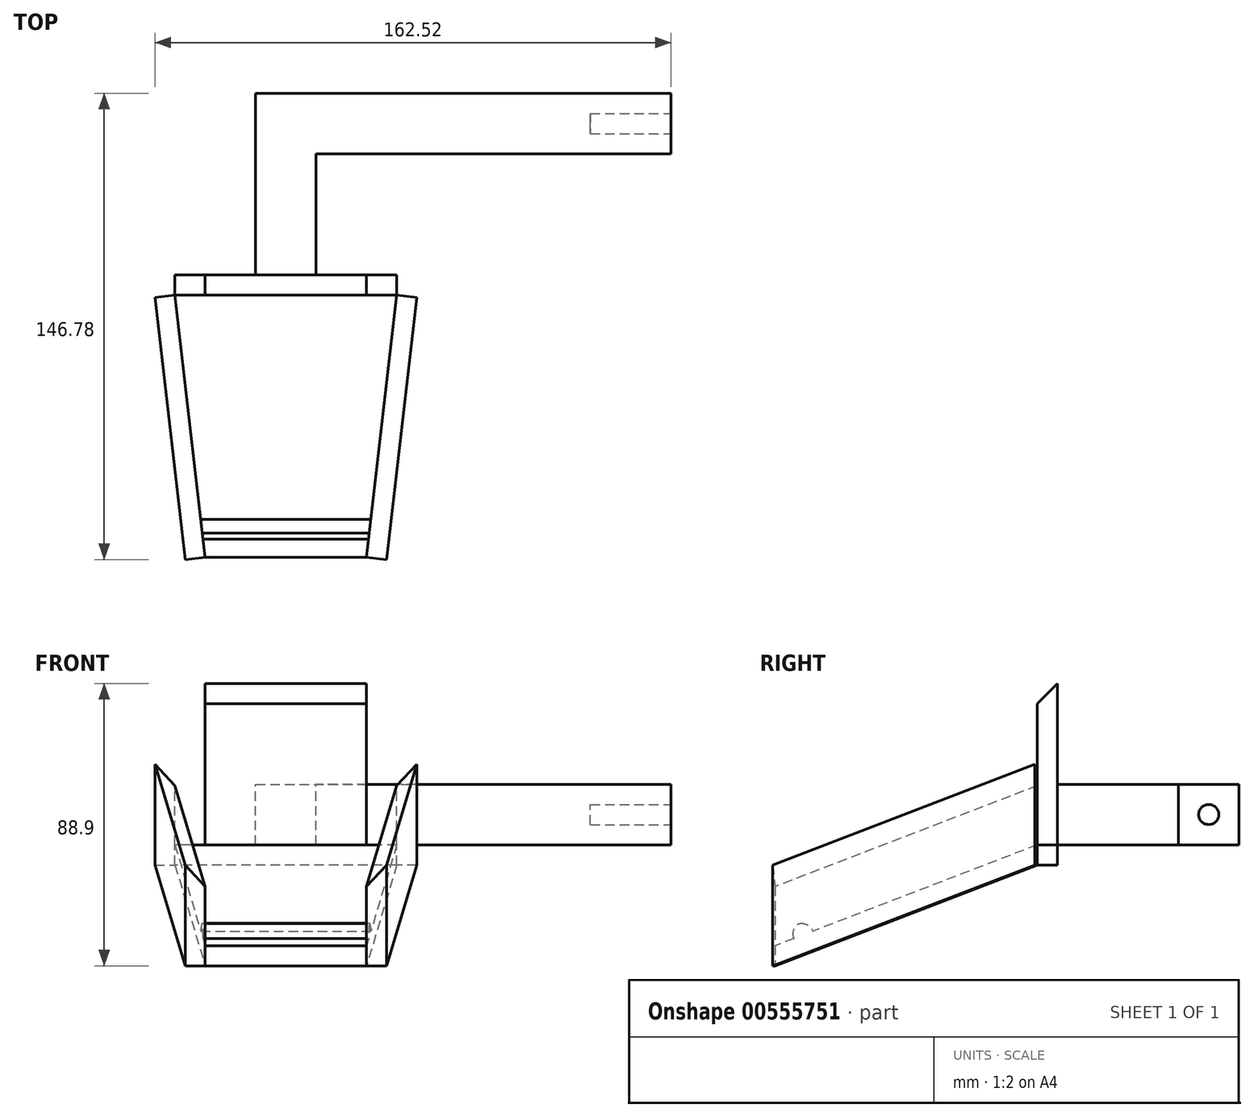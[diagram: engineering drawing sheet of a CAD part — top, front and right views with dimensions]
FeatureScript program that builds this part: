
annotation { "Feature Type Name" : "Feature", "Feature Type Description" : "" }
export const myFeature = defineFeature(function(context is Context, id is Id, definition is map)
    precondition{}
    {
        {
            var Q0;
            Q0=qCreatedBy(makeId("Front.planeOp"),FACE);
            var sketch = newSketch(context, id + "F0", { "sketchPlane" : qUnion([Q0])});
            skLineSegment(sketch, "E0.bottom", {"start": v(0, 0) * mm, "end": v(-69.85, 0) * mm});
            skLineSegment(sketch, "E0.top", {"start": v(0, 6.35) * mm, "end": v(-69.85, 6.35) * mm});
            skLineSegment(sketch, "E0.left", {"start": v(0, 0) * mm, "end": v(0, 6.35) * mm});
            skLineSegment(sketch, "E0.right", {"start": v(-69.85, 0) * mm, "end": v(-69.85, 6.35) * mm});
            skSolve(sketch);
        }
        {
            var Q0;
            Q0=makeQuery(id+"F0.imprint","IMPRINT",FACE,{"disambiguationData":[TD([[makeQuery(id+"F0.imprint","IMPRINT",EDGE,{"derivedFrom":sQuery(id+"F0.wireOp",EDGE,"E0.bottom")}),-1.0]])]});
            cPlane(context, id + "F1", {"entities" : qUnion([Q0]), "cplaneType" : CPlaneType.OFFSET, "offset" : 82.55 * mm, "width" : 152.4 * mm, "height" : 152.4 * mm});
        }
        {
            var Q0;
            Q0=qCreatedBy(id+"F1.planeOp",FACE);
            var sketch = newSketch(context, id + "F2", { "sketchPlane" : qUnion([Q0])});
            skLineSegment(sketch, "E1.bottom", {"start": v(-60.33, -25.4) * mm, "end": v(-9.52, -25.4) * mm});
            skLineSegment(sketch, "E1.top", {"start": v(-60.33, -31.75) * mm, "end": v(-9.52, -31.75) * mm});
            skLineSegment(sketch, "E1.left", {"start": v(-60.33, -25.4) * mm, "end": v(-60.33, -31.75) * mm});
            skLineSegment(sketch, "E1.right", {"start": v(-9.53, -25.4) * mm, "end": v(-9.52, -31.75) * mm});
            skSolve(sketch);
        }
        {
            var Q0;
            Q0=makeQuery(id+"F0.imprint","IMPRINT",FACE,{"disambiguationData":[TD([[makeQuery(id+"F0.imprint","IMPRINT",EDGE,{"derivedFrom":sQuery(id+"F0.wireOp",EDGE,"E0.bottom")}),-1.0]])]});
            var Q1;
            Q1=makeQuery(id+"F2.imprint","IMPRINT",FACE,{"disambiguationData":[TD([[makeQuery(id+"F2.imprint","IMPRINT",EDGE,{"derivedFrom":sQuery(id+"F2.wireOp",EDGE,"E1.bottom")}),-1.0]])]});
            loft(context, id + "F3", {"sheetProfilesArray" : [{ "sheetProfileEntities" : qUnion([Q0]) }, { "sheetProfileEntities" : qUnion([Q1]) }]});
        }
        {
            var Q0;
            Q0=makeQuery(id+"F3.opLoft","SWEPT_FACE",FACE,{"disambiguationData":[OSD([sQuery(id+"F0.wireOp",EDGE,"E0.bottom"),sQuery(id+"F0.wireOp",EDGE,"E0.top"),sQuery(id+"F0.wireOp",EDGE,"E0.right"),sQuery(id+"F2.wireOp",EDGE,"E1.bottom"),sQuery(id+"F2.wireOp",EDGE,"E1.top"),sQuery(id+"F2.wireOp",EDGE,"E1.left")])]});
            var sketch = newSketch(context, id + "F4", { "sketchPlane" : qUnion([Q0])});
            skLineSegment(sketch, "E2", {"start": v(-8, 6.35) * mm, "end": v(-8, 31.75) * mm});
            skLineSegment(sketch, "E3", {"start": v(75.1, -25.4) * mm, "end": v(75.1, 0) * mm});
            skLineSegment(sketch, "E4", {"start": v(75.1, 0) * mm, "end": v(-8, 31.75) * mm});
            skLineSegment(sketch, "E5", {"start": v(-8, 0) * mm, "end": v(-8, 6.35) * mm});
            skLineSegment(sketch, "E6", {"start": v(-8, 0) * mm, "end": v(75.1, -31.75) * mm});
            skLineSegment(sketch, "E7", {"start": v(75.1, -31.75) * mm, "end": v(75.1, -25.4) * mm});
            skSolve(sketch);
        }
        {
            var Q0;
            Q0=makeQuery(id+"F4.imprint","IMPRINT",FACE,{"disambiguationData":[TD([[makeQuery(id+"F4.imprint","IMPRINT",EDGE,{"derivedFrom":sQuery(id+"F4.wireOp",EDGE,"E5")}),1.0]])]});
            var Q1;
            Q1=makeQuery(id+"F4.imprint","IMPRINT",FACE,{"disambiguationData":[TD([[makeQuery(id+"F4.imprint","IMPRINT",EDGE,{"derivedFrom":sQuery(id+"F4.wireOp",EDGE,"E2")}),-1.0]])]});
            extrude(context, id + "F5", {"entities" : qUnion([Q0, Q1]), "operationType" : NewBodyOperationType.ADD, "depth" : 6.35 * mm, "offsetDistance" : 25.4 * mm});
        }
        {
            var Q0;
            Q0=makeQuery(id+"F3.opLoft","SWEPT_FACE",FACE,{"disambiguationData":[OSD([sQuery(id+"F0.wireOp",EDGE,"E0.bottom"),sQuery(id+"F0.wireOp",EDGE,"E0.top"),sQuery(id+"F0.wireOp",EDGE,"E0.left"),sQuery(id+"F2.wireOp",EDGE,"E1.bottom"),sQuery(id+"F2.wireOp",EDGE,"E1.top"),sQuery(id+"F2.wireOp",EDGE,"E1.right")])]});
            var sketch = newSketch(context, id + "F6", { "sketchPlane" : qUnion([Q0])});
            skLineSegment(sketch, "E8", {"start": v(-83.1, -31.75) * mm, "end": v(0, 0) * mm});
            skLineSegment(sketch, "E9", {"start": v(0, 0) * mm, "end": v(0, 31.75) * mm});
            skLineSegment(sketch, "E10", {"start": v(0, 31.75) * mm, "end": v(-83.1, 0) * mm});
            skLineSegment(sketch, "E11", {"start": v(-83.1, 0) * mm, "end": v(-83.1, -31.75) * mm});
            skSolve(sketch);
        }
        {
            var Q0;
            {var subQ2=sQuery(id+"F6.wireOp",EDGE,"E10");Q0=makeQuery(id+"F6.imprint","IMPRINT",FACE,{"disambiguationData":[TD([[makeQuery(id+"F6.imprint","IMPRINT",EDGE,{"derivedFrom":subQ2}),1.0]])]});}
            var Q1;
            {var subQ0=sQuery(id+"F6.wireOp",EDGE,"E8");Q1=makeQuery(id+"F6.imprint","IMPRINT",FACE,{"disambiguationData":[TD([[makeQuery(id+"F6.imprint","IMPRINT",EDGE,{"derivedFrom":subQ0}),-1.0]])]});}
            extrude(context, id + "F7", {"entities" : qUnion([Q0, Q1]), "operationType" : NewBodyOperationType.ADD, "depth" : 6.35 * mm, "offsetDistance" : 25.4 * mm});
        }
        {
            var Q0;
            Q0=makeQuery(id+"F3.opLoft","SWEPT_FACE",FACE,{"disambiguationData":[OSD([sQuery(id+"F0.wireOp",EDGE,"E0.top"),sQuery(id+"F0.wireOp",EDGE,"E0.left"),sQuery(id+"F0.wireOp",EDGE,"E0.right"),sQuery(id+"F2.wireOp",EDGE,"E1.bottom"),sQuery(id+"F2.wireOp",EDGE,"E1.left"),sQuery(id+"F2.wireOp",EDGE,"E1.right")])]});
            var sketch = newSketch(context, id + "F8", { "sketchPlane" : qUnion([Q0])});
            skLineSegment(sketch, "E12", {"start": v(-60.33, -86.17) * mm, "end": v(-61.7, -73.47) * mm});
            skLineSegment(sketch, "E13", {"start": v(-61.7, -73.47) * mm, "end": v(-8.16, -73.47) * mm});
            skLineSegment(sketch, "E14", {"start": v(-8.16, -73.47) * mm, "end": v(-9.53, -86.17) * mm});
            skLineSegment(sketch, "E15", {"start": v(-61, -79.82) * mm, "end": v(-8.84, -79.82) * mm});
            skSolve(sketch);
        }
        {
            var Q0;
            {var subQ0=sQuery(id+"F8.wireOp",EDGE,"E13");Q0=makeQuery(id+"F8.imprint","IMPRINT",FACE,{"disambiguationData":[TD([[makeQuery(id+"F8.imprint","IMPRINT",EDGE,{"derivedFrom":subQ0}),-1.0]])]});}
            extrude(context, id + "F9", {"entities" : qUnion([Q0]), "operationType" : NewBodyOperationType.ADD, "depth" : 3.84 * mm, "offsetDistance" : 25.4 * mm});
        }
        {
            var Q0;
            Q0=makeQuery(id+"F9.opExtrude","CAP_EDGE",EDGE,{"disambiguationData":[OSD([sQuery(id+"F8.wireOp",EDGE,"E15")])],"isStart":false});
            var Q1;
            Q1=makeQuery(id+"F9.opExtrude","CAP_EDGE",EDGE,{"disambiguationData":[OSD([sQuery(id+"F8.wireOp",EDGE,"E13")])],"isStart":false});
            fillet(context, id + "F10", {"entities" : qUnion([Q0, Q1]), "radius" : 3.8 * mm, "tangentPropagation" : true, "allowEdgeOverflow" : false});
        }
        {
            var Q0;
            Q0=makeQuery(id+"F3.opLoft","CAP_FACE",FACE,{"disambiguationData":[OSD([makeQuery(id+"F0.imprint","IMPRINT",FACE,{"disambiguationData":[TD([[makeQuery(id+"F0.imprint","IMPRINT",EDGE,{"derivedFrom":sQuery(id+"F0.wireOp",EDGE,"E0.bottom")}),-1.0]])]})])],"isStart":true});
            var sketch = newSketch(context, id + "F11", { "sketchPlane" : qUnion([Q0])});
            skLineSegment(sketch, "E16.bottom", {"start": v(0, 0) * mm, "end": v(76.2, 0) * mm});
            skLineSegment(sketch, "E16.top", {"start": v(0, 44.45) * mm, "end": v(76.2, 44.45) * mm});
            skLineSegment(sketch, "E16.left", {"start": v(0, 0) * mm, "end": v(0, 44.45) * mm});
            skLineSegment(sketch, "E16.right", {"start": v(76.2, 0) * mm, "end": v(76.2, 44.45) * mm});
            skSolve(sketch);
        }
        {
            var Q0;
            {var subQ0=sQuery(id+"F11.wireOp",EDGE,"E16.bottom");Q0=makeQuery(id+"F11.imprint","IMPRINT",FACE,{"disambiguationData":[TD([[makeQuery(id+"F11.imprint","IMPRINT",EDGE,{"derivedFrom":subQ0}),-1.0]])]});}
            extrude(context, id + "F12", {"entities" : qUnion([Q0]), "operationType" : NewBodyOperationType.ADD, "depth" : 6.35 * mm, "offsetDistance" : 25.4 * mm});
        }
        {
            var Q0;
            Q0=makeQuery(id+"F12.opExtrude","SWEPT_FACE",FACE,{"disambiguationData":[OSD([sQuery(id+"F0.wireOp",EDGE,"E0.top"),sQuery(id+"F0.wireOp",EDGE,"E0.left"),sQuery(id+"F0.wireOp",EDGE,"E0.right")])]});
            var sketch = newSketch(context, id + "F13", { "sketchPlane" : qUnion([Q0])});
            skLineSegment(sketch, "E17.bottom", {"start": v(-9.52, 0) * mm, "end": v(-60.33, 0) * mm});
            skLineSegment(sketch, "E17.top", {"start": v(-9.53, 6.35) * mm, "end": v(-60.33, 6.35) * mm});
            skLineSegment(sketch, "E17.left", {"start": v(-60.33, 6.35) * mm, "end": v(-60.33, 0) * mm});
            skLineSegment(sketch, "E17.right", {"start": v(-9.53, 6.35) * mm, "end": v(-9.52, 0) * mm});
            skSolve(sketch);
        }
        {
            var Q0;
            Q0=makeQuery(id+"F13.imprint","IMPRINT",FACE,{"disambiguationData":[TD([[makeQuery(id+"F13.imprint","IMPRINT",EDGE,{"derivedFrom":sQuery(id+"F13.wireOp",EDGE,"E17.bottom")}),-1.0]])]});
            extrude(context, id + "F14", {"entities" : qUnion([Q0]), "operationType" : NewBodyOperationType.ADD, "depth" : 50.8 * mm, "offsetDistance" : 25.4 * mm});
        }
        {
            var Q0;
            Q0=makeQuery(id+"F14.opExtrude","CAP_EDGE",EDGE,{"disambiguationData":[OSD([sQuery(id+"F13.wireOp",EDGE,"E17.bottom")])],"isStart":false});
            chamfer(context, id + "F15", {"entities" : qUnion([Q0]), "width" : 6.35 * mm, "tangentPropagation" : true});
        }
        {
            var Q0;
            Q0=makeQuery(id+"F14.boolean.opBoolean","MERGE",FACE,{"derivedFrom":[makeQuery(id+"F12.opExtrude","CAP_FACE",FACE,{"disambiguationData":[OSD([sQuery(id+"F0.wireOp",EDGE,"E0.top"),sQuery(id+"F0.wireOp",EDGE,"E0.left"),sQuery(id+"F0.wireOp",EDGE,"E0.right"),sQuery(id+"F11.wireOp",EDGE,"E16.bottom"),sQuery(id+"F11.wireOp",EDGE,"E16.left"),sQuery(id+"F11.wireOp",EDGE,"E16.right")])],"isStart":false}),makeQuery(id+"F14.opExtrude","SWEPT_FACE",FACE,{"disambiguationData":[OSD([sQuery(id+"F13.wireOp",EDGE,"E17.top")])]})]});
            var sketch = newSketch(context, id + "F16", { "sketchPlane" : qUnion([Q0])});
            skLineSegment(sketch, "E18.bottom", {"start": v(44.45, 6.35) * mm, "end": v(25.4, 6.35) * mm});
            skLineSegment(sketch, "E18.top", {"start": v(44.45, 25.4) * mm, "end": v(25.4, 25.4) * mm});
            skLineSegment(sketch, "E18.left", {"start": v(44.45, 6.35) * mm, "end": v(44.45, 25.4) * mm});
            skLineSegment(sketch, "E18.right", {"start": v(25.4, 6.35) * mm, "end": v(25.4, 25.4) * mm});
            skPoint(sketch, "E18.middle", {"position": v(34.92, 15.88) * mm});
            skSolve(sketch);
        }
        {
            var Q0;
            Q0=makeQuery(id+"F16.imprint","IMPRINT",FACE,{"disambiguationData":[TD([[makeQuery(id+"F16.imprint","IMPRINT",EDGE,{"derivedFrom":sQuery(id+"F16.wireOp",EDGE,"E18.bottom")}),-1.0]])]});
            extrude(context, id + "F17", {"entities" : qUnion([Q0]), "operationType" : NewBodyOperationType.ADD, "depth" : 57.15 * mm, "offsetDistance" : 25.4 * mm});
        }
        {
            var Q0;
            Q0=makeQuery(id+"F17.opExtrude","SWEPT_FACE",FACE,{"disambiguationData":[OSD([sQuery(id+"F16.wireOp",EDGE,"E18.right")])]});
            var sketch = newSketch(context, id + "F18", { "sketchPlane" : qUnion([Q0])});
            skLineSegment(sketch, "E19.bottom", {"start": v(63.5, 25.4) * mm, "end": v(44.45, 25.4) * mm});
            skLineSegment(sketch, "E19.top", {"start": v(63.5, 6.35) * mm, "end": v(44.45, 6.35) * mm});
            skLineSegment(sketch, "E19.left", {"start": v(63.5, 25.4) * mm, "end": v(63.5, 6.35) * mm});
            skLineSegment(sketch, "E19.right", {"start": v(44.45, 25.4) * mm, "end": v(44.45, 6.35) * mm});
            skSolve(sketch);
        }
        {
            var Q0;
            Q0=makeQuery(id+"F18.imprint","IMPRINT",FACE,{"disambiguationData":[TD([[makeQuery(id+"F18.imprint","IMPRINT",EDGE,{"derivedFrom":sQuery(id+"F18.wireOp",EDGE,"E19.bottom")}),1.0]])]});
            extrude(context, id + "F19", {"entities" : qUnion([Q0]), "operationType" : NewBodyOperationType.ADD, "depth" : 111.76 * mm, "offsetDistance" : 25.4 * mm});
        }
        {
            var Q0;
            Q0=makeQuery(id+"F5.opExtrude","CAP_EDGE",EDGE,{"disambiguationData":[OSD([sQuery(id+"F4.wireOp",EDGE,"E4")])],"isStart":true});
            var Q1;
            Q1=makeQuery(id+"F7.opExtrude","CAP_EDGE",EDGE,{"disambiguationData":[OSD([sQuery(id+"F6.wireOp",EDGE,"E10")])],"isStart":true});
            chamfer(context, id + "F20", {"entities" : qUnion([Q0, Q1]), "width" : 6.35 * mm, "tangentPropagation" : true});
        }
        {
            var Q0;
            Q0=makeQuery(id+"F19.opExtrude","CAP_FACE",FACE,{"disambiguationData":[OSD([sQuery(id+"F18.wireOp",EDGE,"E19.bottom"),sQuery(id+"F18.wireOp",EDGE,"E19.top"),sQuery(id+"F18.wireOp",EDGE,"E19.left"),sQuery(id+"F18.wireOp",EDGE,"E19.right")])],"isStart":false});
            var sketch = newSketch(context, id + "F21", { "sketchPlane" : qUnion([Q0])});
            skCircle(sketch, "E20", {"center": v(53.98, 15.88) * mm, "radius": 3.18 * mm});
            skPoint(sketch, "E20.centerSnap0", {"position": v(44.45, 15.88) * mm});
            skSolve(sketch);
        }
        {
            var Q0;
            Q0=makeQuery(id+"F21.imprint","IMPRINT",FACE,{"disambiguationData":[TD([[makeQuery(id+"F21.imprint","IMPRINT",EDGE,{"derivedFrom":sQuery(id+"F21.wireOp",EDGE,"E20")}),1.0]])]});
            extrude(context, id + "F22", {"entities" : qUnion([Q0]), "operationType" : NewBodyOperationType.REMOVE, "oppositeDirection" : true, "depth" : 25.4 * mm, "offsetDistance" : 25.4 * mm});
        }
    });
